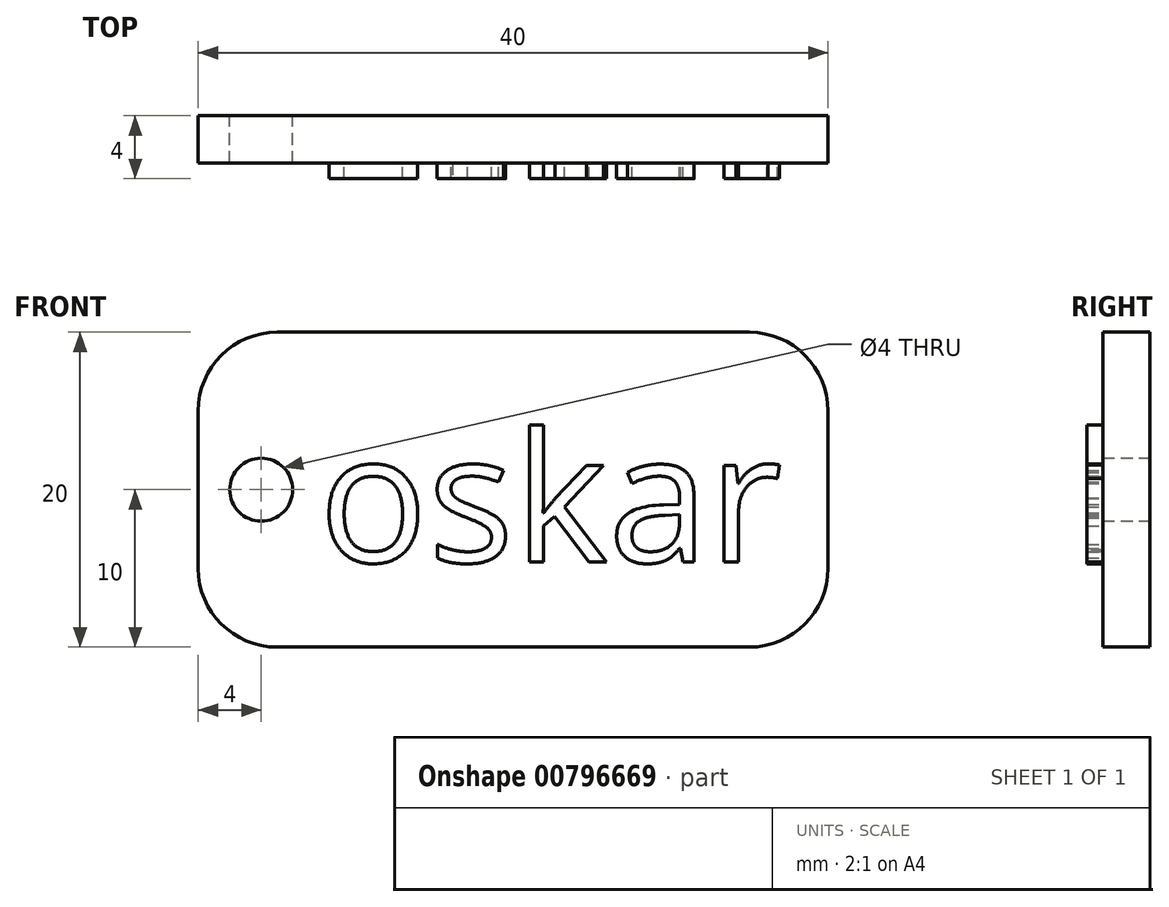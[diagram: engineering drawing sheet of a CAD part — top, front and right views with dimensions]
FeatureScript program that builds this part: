
annotation { "Feature Type Name" : "Feature", "Feature Type Description" : "" }
export const myFeature = defineFeature(function(context is Context, id is Id, definition is map)
    precondition{}
    {
        {
            var Q0;
            Q0=qCreatedBy(makeId("Front.planeOp"),FACE);
            var sketch = newSketch(context, id + "F0", { "sketchPlane" : qUnion([Q0])});
            skLineSegment(sketch, "E0.bottom", {"start": v(5, 20) * mm, "end": v(35, 20) * mm});
            skLineSegment(sketch, "E0.top", {"start": v(5, 0) * mm, "end": v(35, 0) * mm});
            skLineSegment(sketch, "E0.left", {"start": v(0, 15) * mm, "end": v(0, 5) * mm});
            skLineSegment(sketch, "E0.right", {"start": v(40, 15) * mm, "end": v(40, 5) * mm});
            skPoint(sketch, "E1.visualSharp", {"position": v(0, 20) * mm});
            skArc(sketch, "E1.filletArc", {"start": v(5, 20) * mm, "mid": v(1.46, 18.54) * mm, "end": v(0, 15) * mm});
            skPoint(sketch, "E2.visualSharp", {"position": v(0, 0) * mm});
            skArc(sketch, "E2.filletArc", {"start": v(0, 5) * mm, "mid": v(1.46, 1.46) * mm, "end": v(5, 0) * mm});
            skPoint(sketch, "E3.visualSharp", {"position": v(40, 0) * mm});
            skArc(sketch, "E3.filletArc", {"start": v(35, 0) * mm, "mid": v(38.54, 1.46) * mm, "end": v(40, 5) * mm});
            skPoint(sketch, "E4.visualSharp", {"position": v(40, 20) * mm});
            skArc(sketch, "E4.filletArc", {"start": v(40, 15) * mm, "mid": v(38.54, 18.54) * mm, "end": v(35, 20) * mm});
            skSolve(sketch);
        }
        {
            var Q0;
            Q0 = qSketchRegion(id + "F0", true);
            extrude(context, id + "F1", {"entities" : qUnion([Q0]), "depth" : 3 * mm, "offsetDistance" : 25 * mm});
        }
        {
            var Q0;
            Q0=qCreatedBy(makeId("Front.planeOp"),FACE);
            var sketch = newSketch(context, id + "F2", { "sketchPlane" : qUnion([Q0])});
            skCircle(sketch, "E5", {"center": v(4, 10) * mm, "radius": 2 * mm});
            skSolve(sketch);
        }
        {
            var Q0;
            Q0 = qSketchRegion(id + "F2", true);
            extrude(context, id + "F3", {"entities" : qUnion([Q0]), "operationType" : NewBodyOperationType.REMOVE, "oppositeDirection" : true, "depth" : -5 * mm, "offsetDistance" : 25 * mm});
        }
        {
            var Q0;
            Q0=makeQuery(id+"F1.opExtrude","CAP_FACE",FACE,{"disambiguationData":[OSD([sQuery(id+"F0.wireOp",EDGE,"E0.bottom"),sQuery(id+"F0.wireOp",EDGE,"E0.top"),sQuery(id+"F0.wireOp",EDGE,"E0.left"),sQuery(id+"F0.wireOp",EDGE,"E0.right"),sQuery(id+"F0.wireOp",EDGE,"E1.filletArc"),sQuery(id+"F0.wireOp",EDGE,"E2.filletArc"),sQuery(id+"F0.wireOp",EDGE,"E3.filletArc"),sQuery(id+"F0.wireOp",EDGE,"E4.filletArc")])],"isStart":false});
            var sketch = newSketch(context, id + "F4", { "sketchPlane" : qUnion([Q0])});
            skText(sketch, "E6", { "text": "oskar", "fontName": "OpenSans-Regular.ttf"});
            const initialGuessF4  = {"E6": [0.00767, 0.0054, 1, 0, 0.00824]};
            skSetInitialGuess(sketch, initialGuessF4);
            skSolve(sketch);
        }
        {
            var Q0;
            Q0 = qSketchRegion(id + "F4", true);
            extrude(context, id + "F5", {"entities" : qUnion([Q0]), "operationType" : NewBodyOperationType.ADD, "depth" : 1 * mm, "offsetDistance" : 25 * mm});
        }
    });
